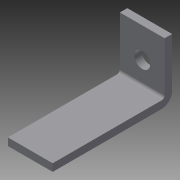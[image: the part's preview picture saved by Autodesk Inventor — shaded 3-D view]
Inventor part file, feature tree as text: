
AUTODESK INVENTOR PART (.ipt)
format: ipt  version: 2013 (Build 170138000, 138)  size: 103,424 bytes
history: native  units: in
note: dims shown in document units (in); Inventor stores cm internally (conversion verified against a paired STEP export)
features: sheet_metal_op x4, sketch x3, other x2, extrude x1
ambient origin geometry x8: Origin, YZ Plane, XZ Plane, XY Plane, X Axis, Y Axis, Z Axis, Center Point
bodies: Solid1 (feature_tree)
feature tree (10):
  sheet_metal_op  "Face1"
  sheet_metal_op  "Flange1"
  extrude  "Extrusion1"  Depth=0.125in
  sketch  "Sketch1"  dims[d0=0.125in d1=0.125in]
  other  "Plate1"
  sketch  "Sketch2"  dims[d2=0.0625in]
  other  "Plate2"
  sheet_metal_op  "Bend1"
  sheet_metal_op  "Corner1"
  sketch  "Sketch3"  dims[d3=0.25in d4=0.125in d5=1.0in d6=90.0deg d7=0.05in d8=0.5in d9=0.125in d10=0.125in d11=1.0in d12=0.0in]
